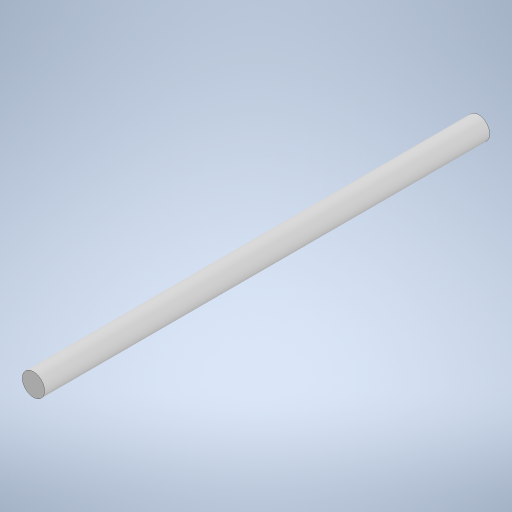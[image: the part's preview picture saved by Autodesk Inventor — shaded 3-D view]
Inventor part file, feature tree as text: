
AUTODESK INVENTOR PART (.ipt)
format: ipt  version: 2024 (Build 280153000, 153)  size: 229,888 bytes
history: native  units: mm
features: extrude x1
ambient origin geometry x8: Origin, YZ Plane, XZ Plane, XY Plane, X Axis, Y Axis, Z Axis, Center Point
bodies: Solid1 (feature_tree)
feature tree (1):
  extrude  "Extrusion1"  Depth=5.0mm
